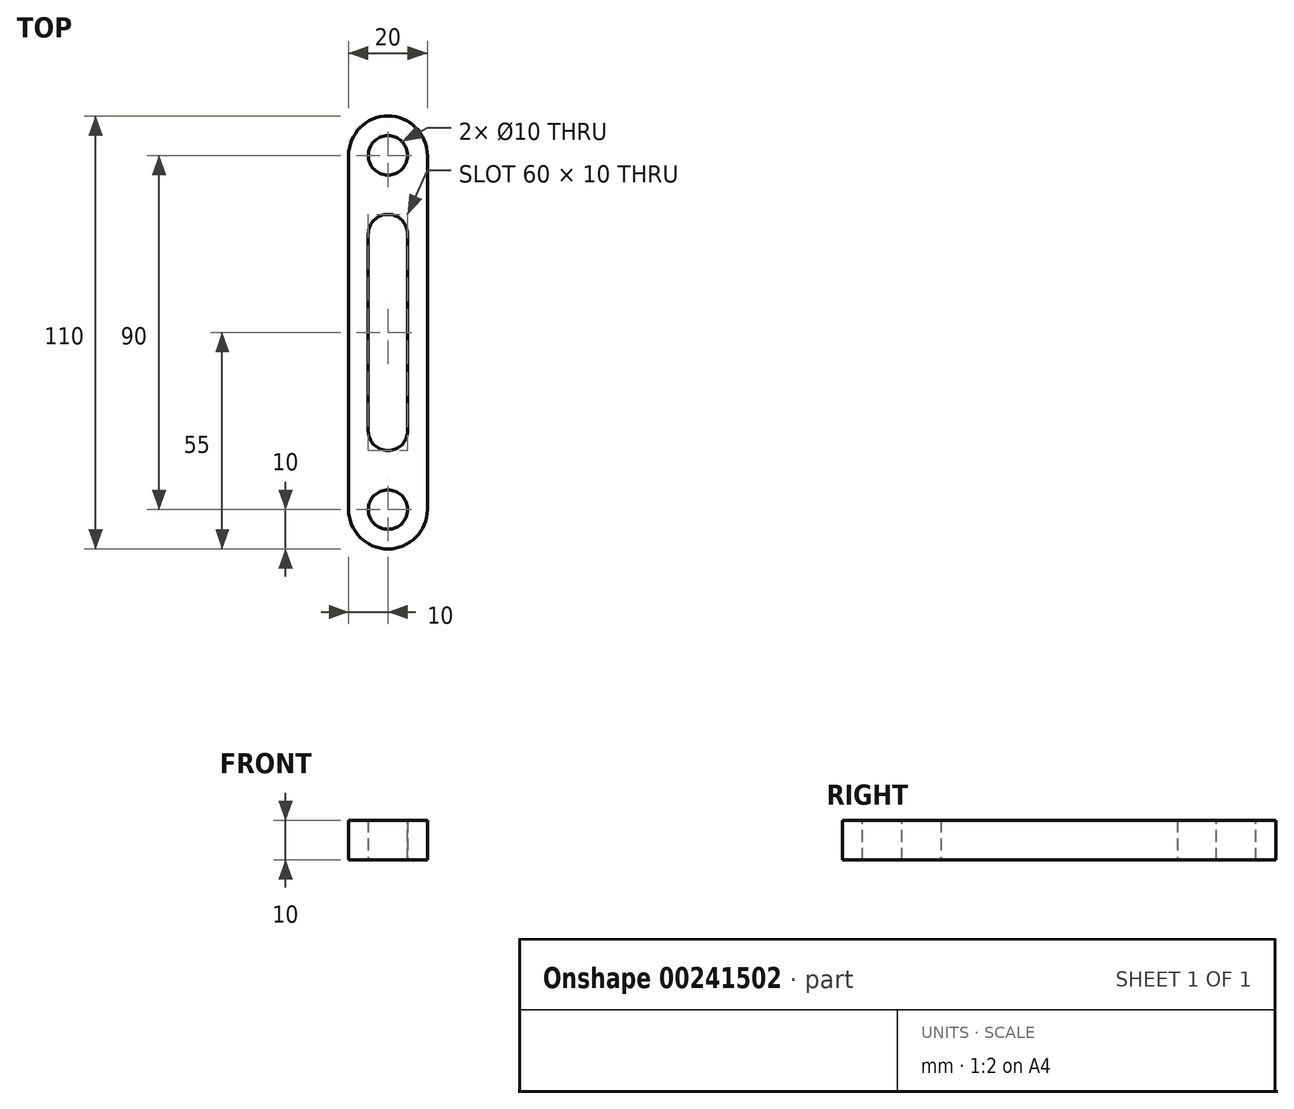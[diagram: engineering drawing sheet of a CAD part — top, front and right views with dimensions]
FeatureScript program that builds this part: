
annotation { "Feature Type Name" : "Feature", "Feature Type Description" : "" }
export const myFeature = defineFeature(function(context is Context, id is Id, definition is map)
    precondition{}
    {
        {
            var Q0;
            Q0=qCreatedBy(makeId("Top.planeOp"),FACE);
            var sketch = newSketch(context, id + "F0", { "sketchPlane" : qUnion([Q0])});
            skArc(sketch, "E0", {"start": v(10, 0) * mm, "mid": v(0, 10) * mm, "end": v(-10, 0) * mm});
            skLineSegment(sketch, "E1", {"start": v(-10, 0) * mm, "end": v(-10, -90) * mm});
            skArc(sketch, "E2", {"start": v(-10, -90) * mm, "mid": v(0, -100) * mm, "end": v(10, -90) * mm});
            skLineSegment(sketch, "E3", {"start": v(10, 0) * mm, "end": v(10, -90) * mm});
            skLineSegment(sketch, "E4.0", {"start": v(5, -20) * mm, "end": v(5, -70) * mm});
            skLineSegment(sketch, "E5.0", {"start": v(-5, -20) * mm, "end": v(-5, -70) * mm});
            skArc(sketch, "E6", {"start": v(5, -20) * mm, "mid": v(0, -15) * mm, "end": v(-5, -20) * mm});
            skArc(sketch, "E7", {"start": v(-5, -70) * mm, "mid": v(0, -75) * mm, "end": v(5, -70) * mm});
            skSolve(sketch);
        }
        {
            var Q0;
            Q0 = qSketchRegion(id + "F0", true);
            extrude(context, id + "F1", {"entities" : qUnion([Q0]), "depth" : 10 * mm});
        }
        {
            var Q0;
            Q0=makeQuery(id+"F1.opExtrude","CAP_FACE",FACE,{"disambiguationData":[OSD([sQuery(id+"F0.wireOp",EDGE,"E0"),sQuery(id+"F0.wireOp",EDGE,"E1"),sQuery(id+"F0.wireOp",EDGE,"E2"),sQuery(id+"F0.wireOp",EDGE,"E3"),sQuery(id+"F0.wireOp",EDGE,"E4.0"),sQuery(id+"F0.wireOp",EDGE,"E5.0"),sQuery(id+"F0.wireOp",EDGE,"E6"),sQuery(id+"F0.wireOp",EDGE,"E7")])],"isStart":false});
            var sketch = newSketch(context, id + "F2", { "sketchPlane" : qUnion([Q0])});
            skPoint(sketch, "E8", {"position": v(0, 0) * mm});
            skPoint(sketch, "E9", {"position": v(0, -90) * mm});
            skSolve(sketch);
        }
        {
            var Q0;
            Q0=sQuery(id+"F2.wireOp",VERTEX,"E8");
            var Q1;
            Q1=sQuery(id+"F2.wireOp",VERTEX,"E9");
            var Q2;
            Q2=makeQuery(id+"F1.opExtrude","SWEPT_BODY",BODY,{"disambiguationData":[OSD([sQuery(id+"F0.wireOp",EDGE,"E0"),sQuery(id+"F0.wireOp",EDGE,"E1"),sQuery(id+"F0.wireOp",EDGE,"E2"),sQuery(id+"F0.wireOp",EDGE,"E3"),sQuery(id+"F0.wireOp",EDGE,"E4.0"),sQuery(id+"F0.wireOp",EDGE,"E5.0"),sQuery(id+"F0.wireOp",EDGE,"E6"),sQuery(id+"F0.wireOp",EDGE,"E7")])]});
            hole(context, id + "F3", {"style" : HoleStyle.SIMPLE, "endStyle" : HoleEndStyle.THROUGH, "holeDiameter" : 10 * mm, "startFromSketch" : true, "locations" : qUnion([Q0, Q1]), "scope" : qUnion([Q2]), "isTappedThrough" : true});
        }
    });
